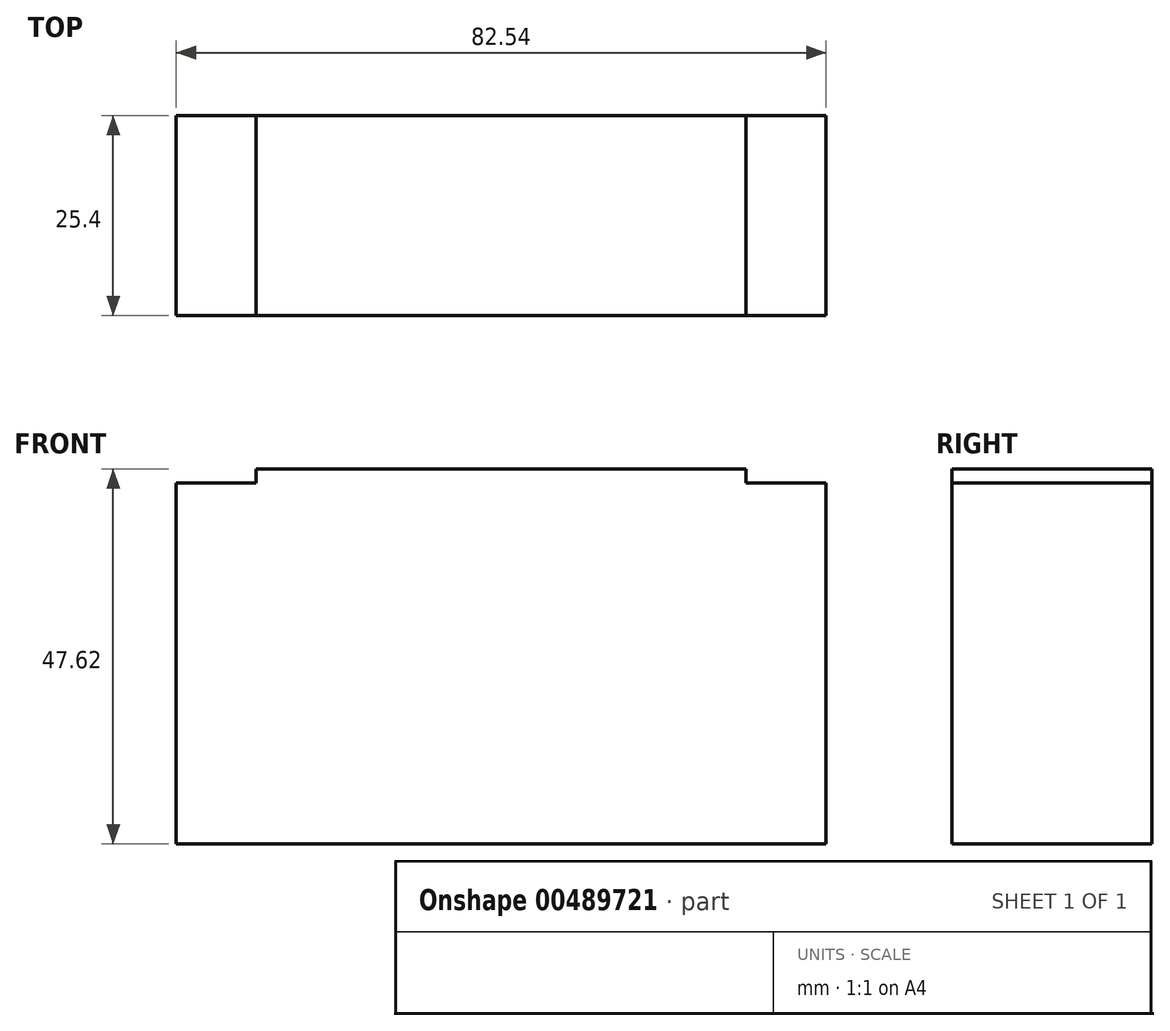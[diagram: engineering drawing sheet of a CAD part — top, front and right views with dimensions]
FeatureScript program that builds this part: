
annotation { "Feature Type Name" : "Feature", "Feature Type Description" : "" }
export const myFeature = defineFeature(function(context is Context, id is Id, definition is map)
    precondition{}
    {
        {
            var Q0;
            Q0=qCreatedBy(makeId("Front.planeOp"),FACE);
            var sketch = newSketch(context, id + "F0", { "sketchPlane" : qUnion([Q0])});
            skLineSegment(sketch, "E0.bottom", {"start": v(31.11, 23.81) * mm, "end": v(-31.12, 23.81) * mm});
            skLineSegment(sketch, "E0.top", {"start": v(41.28, -23.81) * mm, "end": v(-41.28, -23.81) * mm});
            skLineSegment(sketch, "E0.left", {"start": v(41.28, 22.03) * mm, "end": v(41.28, -23.81) * mm});
            skLineSegment(sketch, "E0.right", {"start": v(-41.28, 22.03) * mm, "end": v(-41.28, -23.81) * mm});
            skPoint(sketch, "E0.middle", {"position": v(0, 0) * mm});
            skLineSegment(sketch, "E1.top", {"start": v(-41.28, 22.03) * mm, "end": v(-31.12, 22.03) * mm});
            skLineSegment(sketch, "E1.right", {"start": v(-31.12, 23.81) * mm, "end": v(-31.12, 22.03) * mm});
            skLineSegment(sketch, "E2.top", {"start": v(41.27, 22.03) * mm, "end": v(31.11, 22.03) * mm});
            skLineSegment(sketch, "E2.right", {"start": v(31.11, 23.81) * mm, "end": v(31.11, 22.03) * mm});
            skPoint(sketch, "E3.orphan", {"position": v(-41.28, 23.81) * mm});
            skPoint(sketch, "E4.orphan", {"position": v(41.28, 23.81) * mm});
            skSolve(sketch);
        }
        {
            var Q0;
            Q0 = qSketchRegion(id + "F0", true);
            extrude(context, id + "F1", {"entities" : qUnion([Q0]), "depth" : 25.4 * mm});
        }
    });
